# Revit family: WC-Close Coupled-Caroma Profile 5 Deluxe Integrated Basin Suite1
name_source: partatom
category: Plumbing Fixtures
revit_build: Autodesk Revit 2014 (Build: 20131024_2115(x64)
units: mm (PartAtom-declared; Revit-internal decimal feet)

## types (1)
- Standard
    Assembly Code = D2010110
    CW Connection = Yes
    CWFU = 1.18
    Caroma Fittings = Caroma - Chrome
    Caroma Material = Caroma - Vitreous China
    Default Elevation = 0 mm  [stored 0 ft]
    Description = Caroma Profile 5 Deluxe with Integrated Hand Basin
    HW Connection = No
    Hardware = Metal-Chrome-Caroma
    Height_ANZRS = 935 mm
    Keynote = WC
    Length_ANZRS = 660 mm
    Manufacturer = GWA Bathrooms & Kitchens
    Material_ANZRS = Porcelain-White-Caroma
    Model = 977785W
    ModifiedIssue_ANZRS = 20140919.02 $
    Type Comments = White Only, S or P Trap, Bottom Inlet Cistern
    URL = http://www.caroma.com.au
    Vent Connection = No
    WELSRating_ANZRS = WELS 4 Star rated, 4.5/3L
    WFU = 1.18
    Waste Connection = Yes
    WasteOutlet_ANZRS = 0
    Width_ANZRS = 395 mm  [stored 1.29593 ft]

note: [stored X ft] marks values corroborated as IEEE doubles in the binary element streams (Revit-internal decimal feet)

## geometry (parser evidence)
native form markers: Blend x18, Sweep x1
no freeform markers — native parametric forms only
